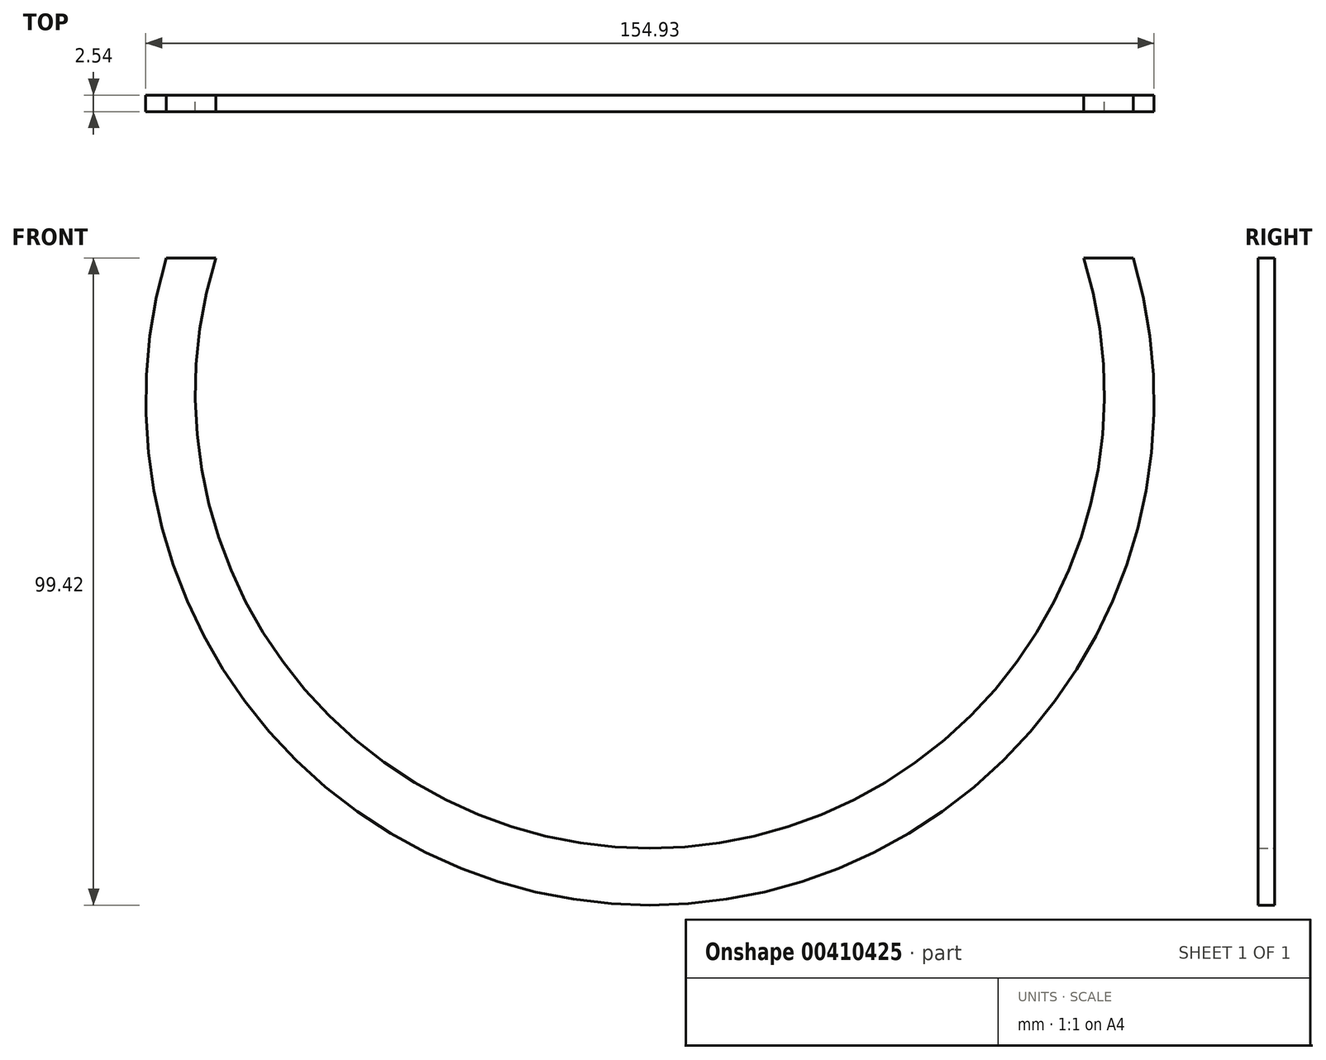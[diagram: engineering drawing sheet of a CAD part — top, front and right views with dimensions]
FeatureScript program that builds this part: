
annotation { "Feature Type Name" : "Feature", "Feature Type Description" : "" }
export const myFeature = defineFeature(function(context is Context, id is Id, definition is map)
    precondition{}
    {
        {
            var Q0;
            Q0=qCreatedBy(makeId("Front.planeOp"),FACE);
            var sketch = newSketch(context, id + "F0", { "sketchPlane" : qUnion([Q0])});
            skLineSegment(sketch, "E0", {"start": v(0, 0) * mm, "end": v(7.62, 0) * mm});
            skLineSegment(sketch, "E1", {"start": v(140.97, 0) * mm, "end": v(148.6, 0) * mm});
            skPoint(sketch, "E1.startSnap0", {"position": v(3.81, 0) * mm});
            skPoint(sketch, "E1.endSnap0", {"position": v(3.81, 0) * mm});
            skArc(sketch, "E2", {"start": v(7.62, 0) * mm, "mid": v(74.3, -90.67) * mm, "end": v(140.97, 0) * mm});
            skArc(sketch, "E3", {"start": v(0, 0) * mm, "mid": v(74.3, -99.42) * mm, "end": v(148.6, 0) * mm});
            skSolve(sketch);
        }
        {
            var Q0;
            Q0 = qSketchRegion(id + "F0", true);
            extrude(context, id + "F1", {"entities" : qUnion([Q0]), "depth" : 2.54 * mm});
        }
    });
